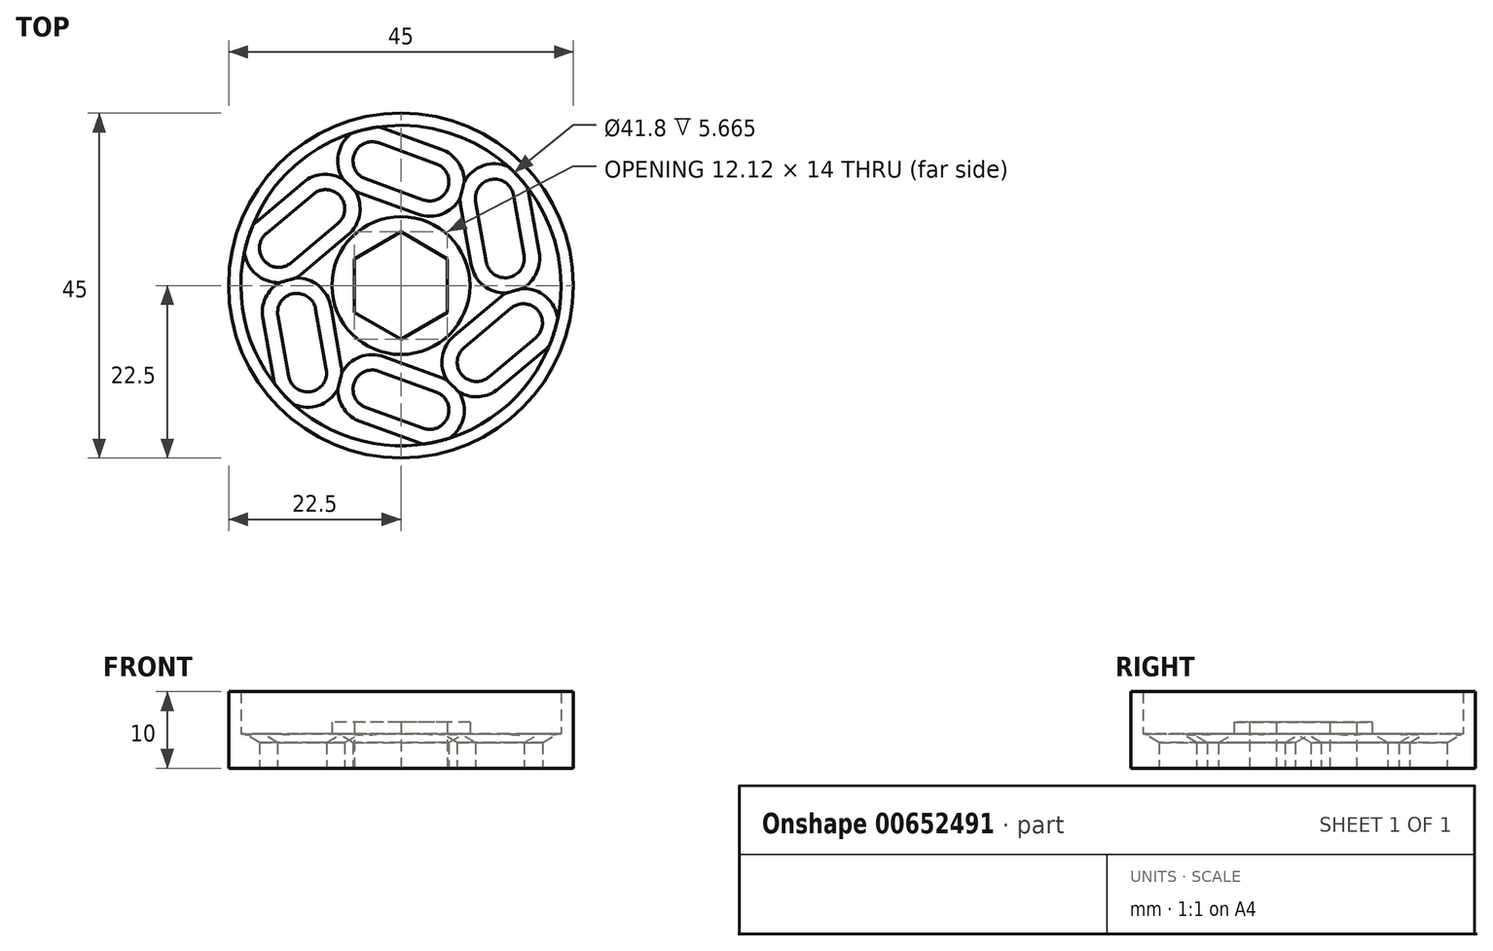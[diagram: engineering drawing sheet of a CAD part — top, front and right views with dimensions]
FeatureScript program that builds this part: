
annotation { "Feature Type Name" : "Feature", "Feature Type Description" : "" }
export const myFeature = defineFeature(function(context is Context, id is Id, definition is map)
    precondition{}
    {
        {
            var Q0;
            Q0=qCreatedBy(makeId("Top.planeOp"),FACE);
            var sketch = newSketch(context, id + "F0", { "sketchPlane" : qUnion([Q0])});
            skCircle(sketch, "E0", {"center": v(0, 0) * mm, "radius": 22.5 * mm});
            skCircle(sketch, "E1", {"center": v(0, 0) * mm, "radius": 25 * mm});
            skCircle(sketch, "E2", {"center": v(0, 0) * mm, "radius": 7 * mm});
            skCircle(sketch, "E3", {"center": v(0, 0) * mm, "radius": 8 * mm});
            skCircle(sketch, "E4", {"center": v(0, 0) * mm, "radius": 9 * mm});
            skCircle(sketch, "E5", {"center": v(0, 0) * mm, "radius": 20.9 * mm});
            skLineSegment(sketch, "E6", {"start": v(2.9, -18.62) * mm, "end": v(-4.61, -15.88) * mm});
            skLineSegment(sketch, "E7", {"start": v(-2.9, -11.18) * mm, "end": v(4.61, -13.92) * mm});
            skArc(sketch, "E8", {"start": v(-2.9, -11.18) * mm, "mid": v(-6.1, -12.68) * mm, "end": v(-4.61, -15.88) * mm});
            skArc(sketch, "E9", {"start": v(2.9, -18.62) * mm, "mid": v(6.1, -17.12) * mm, "end": v(4.61, -13.92) * mm});
            skPoint(sketch, "E10", {"position": v(0.86, -12.55) * mm});
            skPoint(sketch, "E11", {"position": v(-0.86, -17.25) * mm});
            skLineSegment(sketch, "E12", {"start": v(0.86, -12.55) * mm, "end": v(-0.86, -17.25) * mm, "construction": true});
            skLineSegment(sketch, "E13", {"start": v(3.76, -16.27) * mm, "end": v(-3.76, -13.53) * mm, "construction": true});
            skPoint(sketch, "E14", {"position": v(0, -14.9) * mm});
            skPoint(sketch, "E15.1.0", {"position": v(11.3, -5.53) * mm});
            skLineSegment(sketch, "E15.1.1", {"start": v(11.3, -5.53) * mm, "end": v(14.51, -9.37) * mm, "construction": true});
            skLineSegment(sketch, "E15.1.2", {"start": v(15.97, -4.88) * mm, "end": v(9.84, -10.02) * mm, "construction": true});
            skLineSegment(sketch, "E15.1.3", {"start": v(17.57, -6.8) * mm, "end": v(11.45, -11.94) * mm});
            skLineSegment(sketch, "E15.1.4", {"start": v(8.23, -8.1) * mm, "end": v(14.36, -2.96) * mm});
            skPoint(sketch, "E15.1.5", {"position": v(12.9, -7.45) * mm});
            skPoint(sketch, "E15.1.6", {"position": v(14.51, -9.37) * mm});
            skArc(sketch, "E15.1.7", {"start": v(8.23, -8.1) * mm, "mid": v(7.92, -11.63) * mm, "end": v(11.45, -11.94) * mm});
            skArc(sketch, "E15.1.8", {"start": v(17.57, -6.8) * mm, "mid": v(17.88, -3.27) * mm, "end": v(14.36, -2.96) * mm});
            skPoint(sketch, "E15.1.9", {"position": v(11.3, -5.53) * mm});
            skPoint(sketch, "E15.2.0", {"position": v(10.44, 7.02) * mm});
            skLineSegment(sketch, "E15.2.1", {"start": v(10.44, 7.02) * mm, "end": v(15.37, 7.88) * mm, "construction": true});
            skLineSegment(sketch, "E15.2.2", {"start": v(12.2, 11.39) * mm, "end": v(13.6, 3.51) * mm, "construction": true});
            skLineSegment(sketch, "E15.2.3", {"start": v(14.67, 11.82) * mm, "end": v(16.06, 3.94) * mm});
            skLineSegment(sketch, "E15.2.4", {"start": v(11.14, 3.08) * mm, "end": v(9.75, 10.96) * mm});
            skPoint(sketch, "E15.2.5", {"position": v(12.9, 7.45) * mm});
            skPoint(sketch, "E15.2.6", {"position": v(15.37, 7.88) * mm});
            skArc(sketch, "E15.2.7", {"start": v(11.14, 3.08) * mm, "mid": v(14.03, 1.05) * mm, "end": v(16.06, 3.94) * mm});
            skArc(sketch, "E15.2.8", {"start": v(14.67, 11.82) * mm, "mid": v(11.78, 13.85) * mm, "end": v(9.75, 10.96) * mm});
            skPoint(sketch, "E15.2.9", {"position": v(10.44, 7.02) * mm});
            skPoint(sketch, "E15.3.0", {"position": v(-0.86, 12.55) * mm});
            skLineSegment(sketch, "E15.3.1", {"start": v(-0.86, 12.55) * mm, "end": v(0.86, 17.25) * mm, "construction": true});
            skLineSegment(sketch, "E15.3.2", {"start": v(-3.76, 16.27) * mm, "end": v(3.76, 13.53) * mm, "construction": true});
            skLineSegment(sketch, "E15.3.3", {"start": v(-2.9, 18.62) * mm, "end": v(4.61, 15.88) * mm});
            skLineSegment(sketch, "E15.3.4", {"start": v(2.9, 11.18) * mm, "end": v(-4.61, 13.92) * mm});
            skPoint(sketch, "E15.3.5", {"position": v(0, 14.9) * mm});
            skPoint(sketch, "E15.3.6", {"position": v(0.86, 17.25) * mm});
            skArc(sketch, "E15.3.7", {"start": v(2.9, 11.18) * mm, "mid": v(6.1, 12.68) * mm, "end": v(4.61, 15.88) * mm});
            skArc(sketch, "E15.3.8", {"start": v(-2.9, 18.62) * mm, "mid": v(-6.1, 17.12) * mm, "end": v(-4.61, 13.92) * mm});
            skPoint(sketch, "E15.3.9", {"position": v(-0.86, 12.55) * mm});
            skPoint(sketch, "E16", {"position": v(-6.1, -12.68) * mm});
            skPoint(sketch, "E17", {"position": v(6.1, -17.12) * mm});
            skLineSegment(sketch, "E18.1.4.0", {"start": v(-11.3, 5.53) * mm, "end": v(-14.51, 9.37) * mm, "construction": true});
            skLineSegment(sketch, "E18.4.4.0", {"start": v(-15.97, 4.88) * mm, "end": v(-9.84, 10.02) * mm, "construction": true});
            skLineSegment(sketch, "E18.7.4.0", {"start": v(-17.57, 6.8) * mm, "end": v(-11.45, 11.94) * mm});
            skPoint(sketch, "E18.9.4.0", {"position": v(-11.3, 5.53) * mm});
            skLineSegment(sketch, "E18.10.4.0", {"start": v(-8.23, 8.1) * mm, "end": v(-14.36, 2.96) * mm});
            skPoint(sketch, "E18.13.4.0", {"position": v(-12.9, 7.45) * mm});
            skPoint(sketch, "E18.14.4.0", {"position": v(-14.51, 9.37) * mm});
            skArc(sketch, "E18.15.4.0", {"start": v(-8.23, 8.1) * mm, "mid": v(-7.92, 11.63) * mm, "end": v(-11.45, 11.94) * mm});
            skArc(sketch, "E18.19.4.0", {"start": v(-17.57, 6.8) * mm, "mid": v(-17.88, 3.27) * mm, "end": v(-14.36, 2.96) * mm});
            skPoint(sketch, "E18.23.4.0", {"position": v(-11.3, 5.53) * mm});
            skLineSegment(sketch, "E18.1.5.0", {"start": v(-10.44, -7.02) * mm, "end": v(-15.37, -7.88) * mm, "construction": true});
            skLineSegment(sketch, "E18.4.5.0", {"start": v(-12.2, -11.39) * mm, "end": v(-13.6, -3.51) * mm, "construction": true});
            skLineSegment(sketch, "E18.7.5.0", {"start": v(-14.67, -11.82) * mm, "end": v(-16.06, -3.94) * mm});
            skPoint(sketch, "E18.9.5.0", {"position": v(-10.44, -7.02) * mm});
            skLineSegment(sketch, "E18.10.5.0", {"start": v(-11.14, -3.08) * mm, "end": v(-9.75, -10.96) * mm});
            skPoint(sketch, "E18.13.5.0", {"position": v(-12.9, -7.45) * mm});
            skPoint(sketch, "E18.14.5.0", {"position": v(-15.37, -7.88) * mm});
            skArc(sketch, "E18.15.5.0", {"start": v(-11.14, -3.08) * mm, "mid": v(-14.03, -1.05) * mm, "end": v(-16.06, -3.94) * mm});
            skArc(sketch, "E18.19.5.0", {"start": v(-14.67, -11.82) * mm, "mid": v(-11.78, -13.85) * mm, "end": v(-9.75, -10.96) * mm});
            skPoint(sketch, "E18.23.5.0", {"position": v(-10.44, -7.02) * mm});
            skCircle(sketch, "E19.cCircle", {"center": v(0, 0) * mm, "radius": 7 * mm, "construction": true});
            skLineSegment(sketch, "E19.0", {"start": v(0, -7) * mm, "end": v(-6.06, -3.5) * mm});
            skLineSegment(sketch, "E19.1", {"start": v(-6.06, -3.5) * mm, "end": v(-6.06, 3.5) * mm});
            skLineSegment(sketch, "E19.2", {"start": v(-6.06, 3.5) * mm, "end": v(0, 7) * mm});
            skLineSegment(sketch, "E19.3", {"start": v(0, 7) * mm, "end": v(6.06, 3.5) * mm});
            skLineSegment(sketch, "E19.4", {"start": v(6.06, 3.5) * mm, "end": v(6.06, -3.5) * mm});
            skLineSegment(sketch, "E19.5", {"start": v(6.06, -3.5) * mm, "end": v(0, -7) * mm});
            skSolve(sketch);
        }
        {
            var Q0;
            {var subQ0=sQuery(id+"F0.wireOp",EDGE,"5EK9sHSC-FVfV-1HNS-Crza-enBdLEMQdr5X");var subQ1=sQuery(id+"F0.wireOp",EDGE,"E0");var subQ2=makeQuery(id+"F0.imprint","INTERSECT",VERTEX,{"derivedFrom":[subQ1,subQ0]});Q0=makeQuery(id+"F0.imprint","IMPRINT",FACE,{"disambiguationData":[TD([[makeQuery(id+"F0.imprint","IMPRINT",EDGE,{"disambiguationData":[TD([[subQ2,1.0]])],"derivedFrom":subQ1}),1.0]])]});}
            var Q1;
            Q1=makeQuery(id+"F0.imprint","IMPRINT",FACE,{"disambiguationData":[TD([[makeQuery(id+"F0.imprint","IMPRINT",EDGE,{"derivedFrom":sQuery(id+"F0.wireOp",EDGE,"E4")}),-1.0]])]});
            var Q2;
            {var subQ1=sQuery(id+"F0.wireOp",EDGE,"5EK9sHSC-FVfV-1HNS-Crza-enBdLEMQdr5X");var subQ9=sQuery(id+"F0.wireOp",EDGE,"QcTdW98K-azaB-VDkS-TvTL-JB9nxtKtSf4R");var subQ10=makeQuery(id+"F0.imprint","INTERSECT",VERTEX,{"derivedFrom":[subQ9,subQ1]});Q2=makeQuery(id+"F0.imprint","IMPRINT",FACE,{"disambiguationData":[TD([[makeQuery(id+"F0.imprint","IMPRINT",EDGE,{"disambiguationData":[TD([[subQ10,1.0]])],"derivedFrom":subQ9}),1.0]])]});}
            var Q3;
            {var subQ0=sQuery(id+"F0.wireOp",EDGE,"5EK9sHSC-FVfV-1HNS-Crza-enBdLEMQdr5X");var subQ1=sQuery(id+"F0.wireOp",EDGE,"E0");var subQ2=makeQuery(id+"F0.imprint","INTERSECT",VERTEX,{"derivedFrom":[subQ1,subQ0]});Q3=makeQuery(id+"F0.imprint","IMPRINT",FACE,{"disambiguationData":[TD([[makeQuery(id+"F0.imprint","IMPRINT",EDGE,{"disambiguationData":[TD([[subQ2,-1.0]])],"derivedFrom":subQ1}),1.0]])]});}
            extrude(context, id + "F1", {"entities" : qUnion([Q0, Q1, Q2, Q3]), "depth" : 6.5 * mm, "offsetDistance" : 25 * mm, "hasSecondDirection" : true, "secondDirectionOppositeDirection" : false, "secondDirectionDepth" : 2 * mm});
        }
        {
            var Q0;
            Q0=makeQuery(id+"F0.imprint","IMPRINT",FACE,{"disambiguationData":[TD([[makeQuery(id+"F0.imprint","IMPRINT",EDGE,{"derivedFrom":sQuery(id+"F0.wireOp",EDGE,"E3")}),-1.0]])]});
            extrude(context, id + "F2", {"entities" : qUnion([Q0]), "operationType" : NewBodyOperationType.ADD, "depth" : 8 * mm, "offsetDistance" : 25 * mm, "hasSecondDirection" : true, "secondDirectionOppositeDirection" : false, "secondDirectionDepth" : 2 * mm});
        }
        {
            var Q0;
            Q0=makeQuery(id+"F0.imprint","IMPRINT",FACE,{"disambiguationData":[TD([[makeQuery(id+"F0.imprint","IMPRINT",EDGE,{"derivedFrom":sQuery(id+"F0.wireOp",EDGE,"E3")}),1.0]])]});
            var Q1;
            {var subQ0=sQuery(id+"F0.wireOp",EDGE,"3adc19d8-ea81-4d13-a8a2-e7773a07d64e.18.0");Q1=makeQuery(id+"F0.imprint","IMPRINT",FACE,{"disambiguationData":[TD([[makeQuery(id+"F0.imprint","IMPRINT",EDGE,{"derivedFrom":subQ0}),1.0]])]});}
            var Q2;
            {var subQ0=sQuery(id+"F0.wireOp",EDGE,"3adc19d8-ea81-4d13-a8a2-e7773a07d64e.16.0");Q2=makeQuery(id+"F0.imprint","IMPRINT",FACE,{"disambiguationData":[TD([[makeQuery(id+"F0.imprint","IMPRINT",EDGE,{"derivedFrom":subQ0}),1.0]])]});}
            var Q3;
            {var subQ0=sQuery(id+"F0.wireOp",EDGE,"3adc19d8-ea81-4d13-a8a2-e7773a07d64e.17.0");Q3=makeQuery(id+"F0.imprint","IMPRINT",FACE,{"disambiguationData":[TD([[makeQuery(id+"F0.imprint","IMPRINT",EDGE,{"derivedFrom":subQ0}),1.0]])]});}
            var Q4;
            {var subQ0=sQuery(id+"F0.wireOp",EDGE,"3adc19d8-ea81-4d13-a8a2-e7773a07d64e.9.0");Q4=makeQuery(id+"F0.imprint","IMPRINT",FACE,{"disambiguationData":[TD([[makeQuery(id+"F0.imprint","IMPRINT",EDGE,{"derivedFrom":subQ0}),1.0]])]});}
            var Q5;
            {var subQ0=sQuery(id+"F0.wireOp",EDGE,"3adc19d8-ea81-4d13-a8a2-e7773a07d64e.10.0");Q5=makeQuery(id+"F0.imprint","IMPRINT",FACE,{"disambiguationData":[TD([[makeQuery(id+"F0.imprint","IMPRINT",EDGE,{"derivedFrom":subQ0}),1.0]])]});}
            var Q6;
            {var subQ0=sQuery(id+"F0.wireOp",EDGE,"3adc19d8-ea81-4d13-a8a2-e7773a07d64e.5.0");Q6=makeQuery(id+"F0.imprint","IMPRINT",FACE,{"disambiguationData":[TD([[makeQuery(id+"F0.imprint","IMPRINT",EDGE,{"derivedFrom":subQ0}),1.0]])]});}
            var Q7;
            {var subQ0=sQuery(id+"F0.wireOp",EDGE,"3adc19d8-ea81-4d13-a8a2-e7773a07d64e.6.0");Q7=makeQuery(id+"F0.imprint","IMPRINT",FACE,{"disambiguationData":[TD([[makeQuery(id+"F0.imprint","IMPRINT",EDGE,{"derivedFrom":subQ0}),1.0]])]});}
            var Q8;
            {var subQ0=sQuery(id+"F0.wireOp",EDGE,"3adc19d8-ea81-4d13-a8a2-e7773a07d64e.3.0");Q8=makeQuery(id+"F0.imprint","IMPRINT",FACE,{"disambiguationData":[TD([[makeQuery(id+"F0.imprint","IMPRINT",EDGE,{"derivedFrom":subQ0}),1.0]])]});}
            var Q9;
            {var subQ0=sQuery(id+"F0.wireOp",EDGE,"3adc19d8-ea81-4d13-a8a2-e7773a07d64e.4.0");Q9=makeQuery(id+"F0.imprint","IMPRINT",FACE,{"disambiguationData":[TD([[makeQuery(id+"F0.imprint","IMPRINT",EDGE,{"derivedFrom":subQ0}),1.0]])]});}
            var Q10;
            {var subQ0=sQuery(id+"F0.wireOp",EDGE,"3adc19d8-ea81-4d13-a8a2-e7773a07d64e.2.0");Q10=makeQuery(id+"F0.imprint","IMPRINT",FACE,{"disambiguationData":[TD([[makeQuery(id+"F0.imprint","IMPRINT",EDGE,{"derivedFrom":subQ0}),1.0]])]});}
            var Q11;
            {var subQ0=sQuery(id+"F0.wireOp",EDGE,"3adc19d8-ea81-4d13-a8a2-e7773a07d64e.1.0");Q11=makeQuery(id+"F0.imprint","IMPRINT",FACE,{"disambiguationData":[TD([[makeQuery(id+"F0.imprint","IMPRINT",EDGE,{"derivedFrom":subQ0}),1.0]])]});}
            var Q12;
            {var subQ0=sQuery(id+"F0.wireOp",EDGE,"c4T46YRO-08C8-fYLe-C9JY-dgvFSxAXlw6J");Q12=makeQuery(id+"F0.imprint","IMPRINT",FACE,{"disambiguationData":[TD([[makeQuery(id+"F0.imprint","IMPRINT",EDGE,{"derivedFrom":subQ0}),1.0]])]});}
            var Q13;
            {var subQ0=sQuery(id+"F0.wireOp",EDGE,"3adc19d8-ea81-4d13-a8a2-e7773a07d64e.19.0");Q13=makeQuery(id+"F0.imprint","IMPRINT",FACE,{"disambiguationData":[TD([[makeQuery(id+"F0.imprint","IMPRINT",EDGE,{"derivedFrom":subQ0}),1.0]])]});}
            var Q14;
            {var subQ0=sQuery(id+"F0.wireOp",EDGE,"3adc19d8-ea81-4d13-a8a2-e7773a07d64e.15.0");Q14=makeQuery(id+"F0.imprint","IMPRINT",FACE,{"disambiguationData":[TD([[makeQuery(id+"F0.imprint","IMPRINT",EDGE,{"derivedFrom":subQ0}),1.0]])]});}
            var Q15;
            {var subQ0=sQuery(id+"F0.wireOp",EDGE,"3adc19d8-ea81-4d13-a8a2-e7773a07d64e.14.0");Q15=makeQuery(id+"F0.imprint","IMPRINT",FACE,{"disambiguationData":[TD([[makeQuery(id+"F0.imprint","IMPRINT",EDGE,{"derivedFrom":subQ0}),1.0]])]});}
            var Q16;
            {var subQ0=sQuery(id+"F0.wireOp",EDGE,"3adc19d8-ea81-4d13-a8a2-e7773a07d64e.13.0");Q16=makeQuery(id+"F0.imprint","IMPRINT",FACE,{"disambiguationData":[TD([[makeQuery(id+"F0.imprint","IMPRINT",EDGE,{"derivedFrom":subQ0}),1.0]])]});}
            var Q17;
            {var subQ0=sQuery(id+"F0.wireOp",EDGE,"3adc19d8-ea81-4d13-a8a2-e7773a07d64e.12.0");Q17=makeQuery(id+"F0.imprint","IMPRINT",FACE,{"disambiguationData":[TD([[makeQuery(id+"F0.imprint","IMPRINT",EDGE,{"derivedFrom":subQ0}),1.0]])]});}
            var Q18;
            {var subQ0=sQuery(id+"F0.wireOp",EDGE,"3adc19d8-ea81-4d13-a8a2-e7773a07d64e.11.0");Q18=makeQuery(id+"F0.imprint","IMPRINT",FACE,{"disambiguationData":[TD([[makeQuery(id+"F0.imprint","IMPRINT",EDGE,{"derivedFrom":subQ0}),1.0]])]});}
            var Q19;
            {var subQ0=sQuery(id+"F0.wireOp",EDGE,"3adc19d8-ea81-4d13-a8a2-e7773a07d64e.8.0");Q19=makeQuery(id+"F0.imprint","IMPRINT",FACE,{"disambiguationData":[TD([[makeQuery(id+"F0.imprint","IMPRINT",EDGE,{"derivedFrom":subQ0}),1.0]])]});}
            var Q20;
            {var subQ0=sQuery(id+"F0.wireOp",EDGE,"3adc19d8-ea81-4d13-a8a2-e7773a07d64e.7.0");Q20=makeQuery(id+"F0.imprint","IMPRINT",FACE,{"disambiguationData":[TD([[makeQuery(id+"F0.imprint","IMPRINT",EDGE,{"derivedFrom":subQ0}),1.0]])]});}
            var Q21;
            {var subQ0=sQuery(id+"F0.wireOp",EDGE,"E19.1");Q21=makeQuery(id+"F0.imprint","IMPRINT",FACE,{"disambiguationData":[TD([[makeQuery(id+"F0.imprint","IMPRINT",EDGE,{"derivedFrom":subQ0}),1.0]])]});}
            var Q22;
            {var subQ0=sQuery(id+"F0.wireOp",EDGE,"E19.2");Q22=makeQuery(id+"F0.imprint","IMPRINT",FACE,{"disambiguationData":[TD([[makeQuery(id+"F0.imprint","IMPRINT",EDGE,{"derivedFrom":subQ0}),1.0]])]});}
            var Q23;
            {var subQ0=sQuery(id+"F0.wireOp",EDGE,"E19.3");Q23=makeQuery(id+"F0.imprint","IMPRINT",FACE,{"disambiguationData":[TD([[makeQuery(id+"F0.imprint","IMPRINT",EDGE,{"derivedFrom":subQ0}),1.0]])]});}
            var Q24;
            {var subQ0=sQuery(id+"F0.wireOp",EDGE,"E19.4");Q24=makeQuery(id+"F0.imprint","IMPRINT",FACE,{"disambiguationData":[TD([[makeQuery(id+"F0.imprint","IMPRINT",EDGE,{"derivedFrom":subQ0}),1.0]])]});}
            var Q25;
            {var subQ0=sQuery(id+"F0.wireOp",EDGE,"E19.5");Q25=makeQuery(id+"F0.imprint","IMPRINT",FACE,{"disambiguationData":[TD([[makeQuery(id+"F0.imprint","IMPRINT",EDGE,{"derivedFrom":subQ0}),1.0]])]});}
            var Q26;
            {var subQ0=sQuery(id+"F0.wireOp",EDGE,"E19.0");Q26=makeQuery(id+"F0.imprint","IMPRINT",FACE,{"disambiguationData":[TD([[makeQuery(id+"F0.imprint","IMPRINT",EDGE,{"derivedFrom":subQ0}),1.0]])]});}
            var Q27;
            {var subQ0=sQuery(id+"F0.wireOp",EDGE,"E4");Q27=makeQuery(id+"F2.boolean.opBoolean","MERGE",FACE,{"derivedFrom":[makeQuery(id+"F1.opExtrude","CAP_FACE",FACE,{"disambiguationData":[OSD([subQ0,sQuery(id+"F0.wireOp",EDGE,"E5"),sQuery(id+"F0.wireOp",EDGE,"E6"),sQuery(id+"F0.wireOp",EDGE,"E7"),sQuery(id+"F0.wireOp",EDGE,"E8"),sQuery(id+"F0.wireOp",EDGE,"E9"),sQuery(id+"F0.wireOp",EDGE,"E15.1.3"),sQuery(id+"F0.wireOp",EDGE,"E15.1.4"),sQuery(id+"F0.wireOp",EDGE,"E15.1.7"),sQuery(id+"F0.wireOp",EDGE,"E15.1.8"),sQuery(id+"F0.wireOp",EDGE,"E15.2.3"),sQuery(id+"F0.wireOp",EDGE,"E15.2.4"),sQuery(id+"F0.wireOp",EDGE,"E15.2.7"),sQuery(id+"F0.wireOp",EDGE,"E15.2.8"),sQuery(id+"F0.wireOp",EDGE,"E15.3.3"),sQuery(id+"F0.wireOp",EDGE,"E15.3.4"),sQuery(id+"F0.wireOp",EDGE,"E15.3.7"),sQuery(id+"F0.wireOp",EDGE,"E15.3.8"),sQuery(id+"F0.wireOp",EDGE,"E18.7.4.0"),sQuery(id+"F0.wireOp",EDGE,"E18.10.4.0"),sQuery(id+"F0.wireOp",EDGE,"E18.15.4.0"),sQuery(id+"F0.wireOp",EDGE,"E18.19.4.0"),sQuery(id+"F0.wireOp",EDGE,"E18.7.5.0"),sQuery(id+"F0.wireOp",EDGE,"E18.10.5.0"),sQuery(id+"F0.wireOp",EDGE,"E18.15.5.0"),sQuery(id+"F0.wireOp",EDGE,"E18.19.5.0")])],"isStart":true}),makeQuery(id+"F2.opExtrude","CAP_FACE",FACE,{"disambiguationData":[OSD([sQuery(id+"F0.wireOp",EDGE,"E3"),subQ0])],"isStart":true})]});}
            extrude(context, id + "F3", {"entities" : qUnion([Q0, Q1, Q2, Q3, Q4, Q5, Q6, Q7, Q8, Q9, Q10, Q11, Q12, Q13, Q14, Q15, Q16, Q17, Q18, Q19, Q20, Q21, Q22, Q23, Q24, Q25, Q26]), "operationType" : NewBodyOperationType.ADD, "depth" : 8 * mm, "offsetDistance" : 25 * mm, "hasSecondDirection" : true, "secondDirectionBound" : SecondDirectionBoundingType.UP_TO_SURFACE, "secondDirectionOppositeDirection" : false, "secondDirectionDepth" : 5 * mm, "secondDirectionBoundEntityFace" : qUnion([Q27])});
        }
        {
            var Q0;
            {var subQ0=sQuery(id+"F0.wireOp",EDGE,"5EK9sHSC-FVfV-1HNS-Crza-enBdLEMQdr5X");var subQ1=sQuery(id+"F0.wireOp",EDGE,"E0");var subQ2=makeQuery(id+"F0.imprint","INTERSECT",VERTEX,{"derivedFrom":[subQ1,subQ0]});Q0=makeQuery(id+"F0.imprint","IMPRINT",FACE,{"disambiguationData":[TD([[makeQuery(id+"F0.imprint","IMPRINT",EDGE,{"disambiguationData":[TD([[subQ2,1.0]])],"derivedFrom":subQ1}),1.0]])]});}
            var Q1;
            {var subQ0=sQuery(id+"F0.wireOp",EDGE,"5EK9sHSC-FVfV-1HNS-Crza-enBdLEMQdr5X");var subQ1=sQuery(id+"F0.wireOp",EDGE,"E0");var subQ2=makeQuery(id+"F0.imprint","INTERSECT",VERTEX,{"derivedFrom":[subQ1,subQ0]});Q1=makeQuery(id+"F0.imprint","IMPRINT",FACE,{"disambiguationData":[TD([[makeQuery(id+"F0.imprint","IMPRINT",EDGE,{"disambiguationData":[TD([[subQ2,-1.0]])],"derivedFrom":subQ1}),1.0]])]});}
            var Q2;
            Q2=makeQuery(id+"F0.imprint","IMPRINT",FACE,{"disambiguationData":[TD([[makeQuery(id+"F0.imprint","IMPRINT",EDGE,{"derivedFrom":sQuery(id+"F0.wireOp",EDGE,"E0")}),1.0]])]});
            extrude(context, id + "F4", {"entities" : qUnion([Q0, Q1, Q2]), "operationType" : NewBodyOperationType.ADD, "depth" : 12 * mm, "offsetDistance" : 25 * mm, "hasSecondDirection" : true, "secondDirectionOppositeDirection" : false, "secondDirectionDepth" : 2 * mm});
        }
        {
            var Q0;
            Q0=makeQuery(id+"F1.opExtrude","CAP_EDGE",EDGE,{"disambiguationData":[OSD([sQuery(id+"F0.wireOp",EDGE,"E7")])],"isStart":false});
            var Q1;
            Q1=makeQuery(id+"F1.opExtrude","CAP_EDGE",EDGE,{"disambiguationData":[OSD([sQuery(id+"F0.wireOp",EDGE,"E15.11.3")])],"isStart":false});
            var Q2;
            Q2=makeQuery(id+"F1.opExtrude","CAP_EDGE",EDGE,{"disambiguationData":[OSD([sQuery(id+"F0.wireOp",EDGE,"E15.10.4")])],"isStart":false});
            var Q3;
            Q3=makeQuery(id+"F1.opExtrude","CAP_EDGE",EDGE,{"disambiguationData":[OSD([sQuery(id+"F0.wireOp",EDGE,"E15.9.4")])],"isStart":false});
            var Q4;
            Q4=makeQuery(id+"F1.opExtrude","CAP_EDGE",EDGE,{"disambiguationData":[OSD([sQuery(id+"F0.wireOp",EDGE,"E15.8.4")])],"isStart":false});
            var Q5;
            Q5=makeQuery(id+"F1.opExtrude","CAP_EDGE",EDGE,{"disambiguationData":[OSD([sQuery(id+"F0.wireOp",EDGE,"E15.7.4")])],"isStart":false});
            var Q6;
            Q6=makeQuery(id+"F1.opExtrude","CAP_EDGE",EDGE,{"disambiguationData":[OSD([sQuery(id+"F0.wireOp",EDGE,"E15.6.4")])],"isStart":false});
            var Q7;
            Q7=makeQuery(id+"F1.opExtrude","CAP_EDGE",EDGE,{"disambiguationData":[OSD([sQuery(id+"F0.wireOp",EDGE,"E15.5.4")])],"isStart":false});
            var Q8;
            Q8=makeQuery(id+"F1.opExtrude","CAP_EDGE",EDGE,{"disambiguationData":[OSD([sQuery(id+"F0.wireOp",EDGE,"E15.4.4")])],"isStart":false});
            var Q9;
            Q9=makeQuery(id+"F1.opExtrude","CAP_EDGE",EDGE,{"disambiguationData":[OSD([sQuery(id+"F0.wireOp",EDGE,"E15.3.4")])],"isStart":false});
            var Q10;
            Q10=makeQuery(id+"F1.opExtrude","CAP_EDGE",EDGE,{"disambiguationData":[OSD([sQuery(id+"F0.wireOp",EDGE,"E15.2.4")])],"isStart":false});
            var Q11;
            Q11=makeQuery(id+"F1.opExtrude","CAP_EDGE",EDGE,{"disambiguationData":[OSD([sQuery(id+"F0.wireOp",EDGE,"E15.1.4")])],"isStart":false});
            var Q12;
            Q12=makeQuery(id+"F1.opExtrude","CAP_EDGE",EDGE,{"disambiguationData":[OSD([sQuery(id+"F0.wireOp",EDGE,"E18.10.4.0")])],"isStart":false});
            var Q13;
            Q13=makeQuery(id+"F1.opExtrude","CAP_EDGE",EDGE,{"disambiguationData":[OSD([sQuery(id+"F0.wireOp",EDGE,"E18.10.5.0")])],"isStart":false});
            chamfer(context, id + "F5", {"entities" : qUnion([Q0, Q1, Q2, Q3, Q4, Q5, Q6, Q7, Q8, Q9, Q10, Q11, Q12, Q13]), "chamferType" : ChamferType.OFFSET_ANGLE, "width" : 2 * mm, "oppositeDirection" : false, "angle" : 30 * degree, "tangentPropagation" : true});
        }
    });
